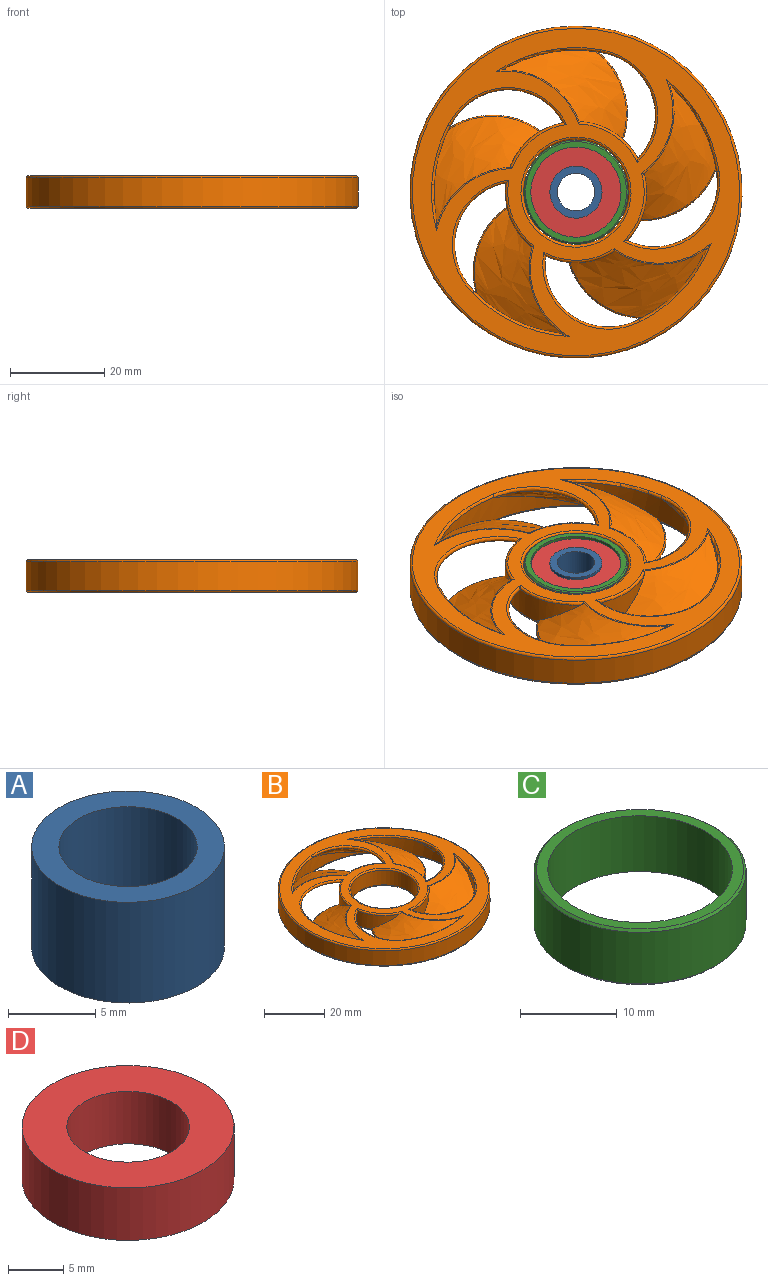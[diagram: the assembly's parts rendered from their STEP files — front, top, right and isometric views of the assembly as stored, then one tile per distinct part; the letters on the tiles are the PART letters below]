
ASSEMBLY  parts=4 mates=1
PART A: 4 faces, bbox 11x11x7.1 mm
  f0: cylinder r=3.96mm len=7.92mm, axis (0,0,-1), area 175.8mm2, adj f2,f3
  f1: cylinder r=5.52mm len=11.05mm, axis (0,0,-1), area 245.1mm2, adj f2,f3
  f2: plane 11.05x11.05mm, normal (0,0,1), area 46.6mm2, adj f0,f1
  f3: plane 11.05x11.05mm, normal (0,0,-1), area 46.6mm2, adj f0,f1
PART B: 68 faces, bbox 76.3x76.3x8 mm
  f0: cylinder r=30.16mm len=36.88mm, axis (0,0,1), area 118.4mm2, adj f15,f22,f55,f57,f59
  f1: cylinder r=30.16mm len=33.71mm, axis (0,0,1), area 118.4mm2, adj f14,f17,f26,f27,f60
  f2: cylinder r=30.16mm len=27.23mm, axis (0,0,1), area 118.4mm2, adj f16,f19,f30,f31,f43
  f3: cylinder r=30.16mm len=32.44mm, axis (0,0,1), area 118.4mm2, adj f18,f21,f34,f35,f47
  f4: cylinder r=30.16mm len=36.44mm, axis (0,0,1), area 118.4mm2, adj f20,f23,f38,f39,f51
  f5: cylinder r=35.24mm len=70.49mm, axis (0,0,1), area 1321.7mm2, adj f66,f67
  f6: plane 69.47x69.47mm, normal (0,0,-1), area 1452mm2, adj f24,f25,f26,f27,f28,f29,f30,f31
  f7: plane 69.47x69.47mm, normal (0,0,1), area 1449.8mm2, adj f40,f41,f42,f43,f44,f45,f46,f47
  f8: cylinder r=14.99mm len=17.21mm, axis (0,0,1), area 84.9mm2, adj f20,f23,f36,f38,f48,f49
  f9: cylinder r=14.99mm len=20.44mm, axis (0,0,1), area 84.9mm2, adj f18,f21,f32,f34,f44,f45
  f10: cylinder r=14.99mm len=21.67mm, axis (0,0,1), area 84.9mm2, adj f16,f19,f28,f30,f40,f41
  f11: cylinder r=14.99mm len=20.78mm, axis (0,0,1), area 84.9mm2, adj f14,f17,f24,f26,f61,f63
  f12: cylinder r=14.99mm len=17.85mm, axis (0,0,1), area 84.9mm2, adj f15,f22,f52,f53,f58,f59
  f13: cylinder r=11.18mm len=22.35mm, axis (0,0,1), area 419.1mm2, adj f64,f65
  f14: bspline ~32.84x17.52mm, area 261.6mm2, adj f1,f11,f26,f60,f62,f63
  f15: bspline ~34.24x32.1mm, area 294mm2, adj f0,f12,f53,f56,f58
  f16: bspline ~30.6x23.26mm, area 261.6mm2, adj f2,f10,f30,f40,f42,f43
  f17: bspline ~38.38x28.82mm, area 294mm2, adj f1,f11,f24,f25,f61
  f18: bspline ~28.76x26.96mm, area 261.6mm2, adj f3,f9,f34,f44,f46,f47
  f19: bspline ~41.17x24.13mm, area 294mm2, adj f2,f10,f28,f29,f41
  f20: bspline ~31.9x22.59mm, area 261.6mm2, adj f4,f8,f38,f48,f50,f51
  f21: bspline ~39.94x21.48mm, area 294mm2, adj f3,f9,f32,f33,f45
  f22: bspline ~33.76x19.02mm, area 261.6mm2, adj f0,f12,f52,f54,f55,f59
  f23: bspline ~34.79x28.04mm, area 294mm2, adj f4,f8,f36,f37,f49
  f24: torus R=14.48mm, axis (0,0,1), area 12.2mm2, adj f6,f11,f17,f25,f26
  f25: bspline ~24.58x11.53mm, area 11.2mm2, adj f6,f17,f24,f27
  f26: bspline ~20.16x14.79mm, area 28.5mm2, adj f1,f6,f11,f14,f24,f27
  f27: torus R=30.67mm, axis (0,0,1), area 17.4mm2, adj f1,f6,f25,f26
  f28: torus R=14.48mm, axis (0,0,1), area 12.2mm2, adj f6,f10,f19,f29,f30
  f29: bspline ~21.53x15.79mm, area 11.2mm2, adj f6,f19,f28,f31
  f30: bspline ~23.53x9.9mm, area 28.5mm2, adj f2,f6,f10,f16,f28,f31
  f31: torus R=30.67mm, axis (0,0,1), area 17.4mm2, adj f2,f6,f29,f30
  f32: torus R=14.48mm, axis (0,0,1), area 12.2mm2, adj f6,f9,f21,f33,f34
  f33: bspline ~19.96x17.49mm, area 11.2mm2, adj f6,f21,f32,f35
  f34: bspline ~24.67x6.72mm, area 28.5mm2, adj f3,f6,f9,f18,f32,f35
  f35: torus R=30.67mm, axis (0,0,1), area 17.4mm2, adj f3,f6,f33,f34
  f36: torus R=14.48mm, axis (0,0,1), area 12.2mm2, adj f6,f8,f23,f37,f38
  f37: bspline ~23.54x13.21mm, area 11.2mm2, adj f6,f23,f36,f39
  f38: bspline ~23.4x10.86mm, area 28.5mm2, adj f4,f6,f8,f20,f36,f39
  f39: torus R=30.67mm, axis (0,0,1), area 17.4mm2, adj f4,f6,f37,f38
  f40: torus R=14.48mm, axis (0,0,1), area 12.2mm2, adj f7,f10,f16,f41,f42
  f41: bspline ~24.21x14.7mm, area 36.8mm2, adj f7,f10,f19,f40,f43
  f42: bspline ~20.08x8.65mm, area 5.5mm2, adj f7,f16,f40,f43
  f43: torus R=30.67mm, axis (0,0,1), area 17.1mm2, adj f2,f7,f16,f41,f42
  f44: torus R=14.48mm, axis (0,0,1), area 12.2mm2, adj f7,f9,f18,f45,f46
  f45: bspline ~26.2x10.78mm, area 36.8mm2, adj f7,f9,f21,f44,f47
  f46: bspline ~16.77x13.63mm, area 5.5mm2, adj f7,f18,f44,f47
  f47: torus R=30.67mm, axis (0,0,1), area 17.1mm2, adj f3,f7,f18,f45,f46
  f48: torus R=14.48mm, axis (0,0,1), area 12.2mm2, adj f7,f8,f20,f49,f50
  f49: bspline ~25.63x12.09mm, area 36.8mm2, adj f7,f8,f23,f48,f51
  f50: bspline ~18.07x11.88mm, area 5.5mm2, adj f7,f20,f48,f51
  f51: torus R=30.67mm, axis (0,0,1), area 17.1mm2, adj f4,f7,f20,f49,f50
  f52: torus R=14.48mm, axis (0,0,1), area 12.2mm2, adj f7,f12,f22,f53,f54
  f53: bspline ~22.69x16.37mm, area 36.8mm2, adj f7,f12,f15,f52,f55
  f54: bspline ~20.73x7.25mm, area 5.5mm2, adj f7,f22,f52,f55
  f55: torus R=30.67mm, axis (0,0,1), area 17.1mm2, adj f0,f7,f22,f53,f54
  f56: bspline ~25.3x9.07mm, area 11.2mm2, adj f6,f15,f57,f58
  f57: torus R=30.67mm, axis (0,0,1), area 17.4mm2, adj f0,f6,f56,f59
  f58: torus R=14.48mm, axis (0,0,1), area 12.2mm2, adj f6,f12,f15,f56,f59
  f59: bspline ~19.83x15.59mm, area 28.5mm2, adj f0,f6,f12,f22,f57,f58
  f60: torus R=30.67mm, axis (0,0,1), area 17.1mm2, adj f1,f7,f14,f61,f62
  f61: bspline ~20.48x18.78mm, area 36.8mm2, adj f7,f11,f17,f60,f63
  f62: bspline ~21.45x4.57mm, area 5.5mm2, adj f7,f14,f60,f63
  f63: torus R=14.48mm, axis (0,0,1), area 12.2mm2, adj f7,f11,f14,f61,f62
  f64: torus R=11.68mm, axis (0,0,1), area 57mm2, adj f7,f13
  f65: torus R=11.68mm, axis (0,0,1), area 57mm2, adj f6,f13
  f66: torus R=34.73mm, axis (0,0,1), area 175.8mm2, adj f5,f7
  f67: torus R=34.73mm, axis (0,0,1), area 175.8mm2, adj f5,f6
PART C: 6 faces, bbox 22x22x7.1 mm
  f0: cylinder r=9.56mm len=19.13mm, axis (0,0,-1), area 424.3mm2, adj f2,f3
  f1: cylinder r=10.99mm len=21.97mm, axis (0,0,-1), area 452.3mm2, adj f4,f5
  f2: plane 21.46x21.46mm, normal (0,0,1), area 74.5mm2, adj f0,f4
  f3: plane 21.46x21.46mm, normal (0,0,-1), area 74.5mm2, adj f0,f5
  f4: cone r=10.73mm half-angle=45deg, axis (0,0,-1), area 24.5mm2, adj f1,f2
  f5: cone r=10.99mm half-angle=45deg, axis (0,0,1), area 24.5mm2, adj f1,f3
PART D: 4 faces, bbox 19.1x19.1x5.8 mm
  f0: cylinder r=5.52mm len=11.05mm, axis (0,0,-1), area 201mm2, adj f2,f3
  f1: cylinder r=9.56mm len=19.13mm, axis (0,0,-1), area 348mm2, adj f2,f3
  f2: plane 19.13x19.13mm, normal (0,0,-1), area 191.4mm2, adj f0,f1
  f3: plane 19.13x19.13mm, normal (0,0,1), area 191.4mm2, adj f0,f1
PLACE A at identity fixed
PLACE B rot(axis=(0,0,1),55deg) t=(0,0,7.02)mm
PLACE C at identity fixed
PLACE D at identity fixed
MATE revolute B.f13 <-> C.f0  axis (0,0,1) through (0,0,3.53)mm
